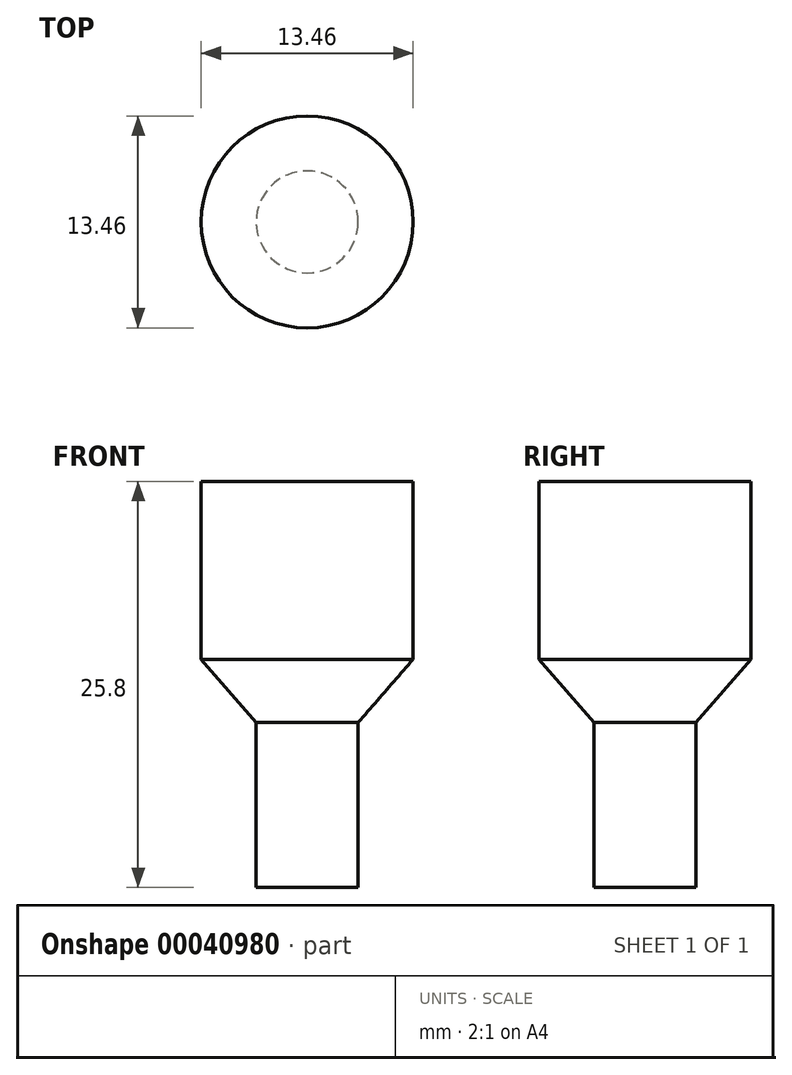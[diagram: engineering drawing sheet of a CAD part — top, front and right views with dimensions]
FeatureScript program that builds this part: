
annotation { "Feature Type Name" : "Feature", "Feature Type Description" : "" }
export const myFeature = defineFeature(function(context is Context, id is Id, definition is map)
    precondition{}
    {
        {
            var Q0;
            Q0=qCreatedBy(makeId("Right.planeOp"),FACE);
            var sketch = newSketch(context, id + "F0", { "sketchPlane" : qUnion([Q0])});
            skLineSegment(sketch, "E0", {"start": v(0, 11.3) * mm, "end": v(0, -14.5) * mm});
            skLineSegment(sketch, "E1", {"start": v(0, -14.5) * mm, "end": v(-3.17, -14.5) * mm});
            skLineSegment(sketch, "E2", {"start": v(-3.17, -14.5) * mm, "end": v(-3.17, -4.09) * mm, "construction": true});
            skLineSegment(sketch, "E3", {"start": v(-3.17, -4.09) * mm, "end": v(-6.73, -4.09) * mm, "construction": true});
            skLineSegment(sketch, "E4", {"start": v(-6.73, 11.3) * mm, "end": v(0, 11.3) * mm});
            skLineSegment(sketch, "E5", {"start": v(-3.18, -4.09) * mm, "end": v(-6.73, 0) * mm});
            skLineSegment(sketch, "E6", {"start": v(-6.73, 0) * mm, "end": v(0, 0) * mm});
            skLineSegment(sketch, "E7", {"start": v(-6.73, 11.3) * mm, "end": v(-6.73, 0) * mm});
            skLineSegment(sketch, "E8", {"start": v(-6.73, -4.09) * mm, "end": v(-6.73, 0) * mm, "construction": true});
            skLineSegment(sketch, "E9", {"start": v(-3.24, -14.5) * mm, "end": v(-3.24, -4.01) * mm});
            skLineSegment(sketch, "E10", {"start": v(0, -14.5) * mm, "end": v(-3.24, -14.5) * mm});
            skSolve(sketch);
        }
        {
            var Q0;
            Q0 = qSketchRegion(id + "F0", true);
            var Q1;
            Q1=sQuery(id+"F0.wireOp",EDGE,"E0");
            revolve(context, id + "F1", {"entities" : qUnion([Q0]), "axis" : qUnion([Q1]), "revolveType" : RevolveType.FULL});
        }
    });
